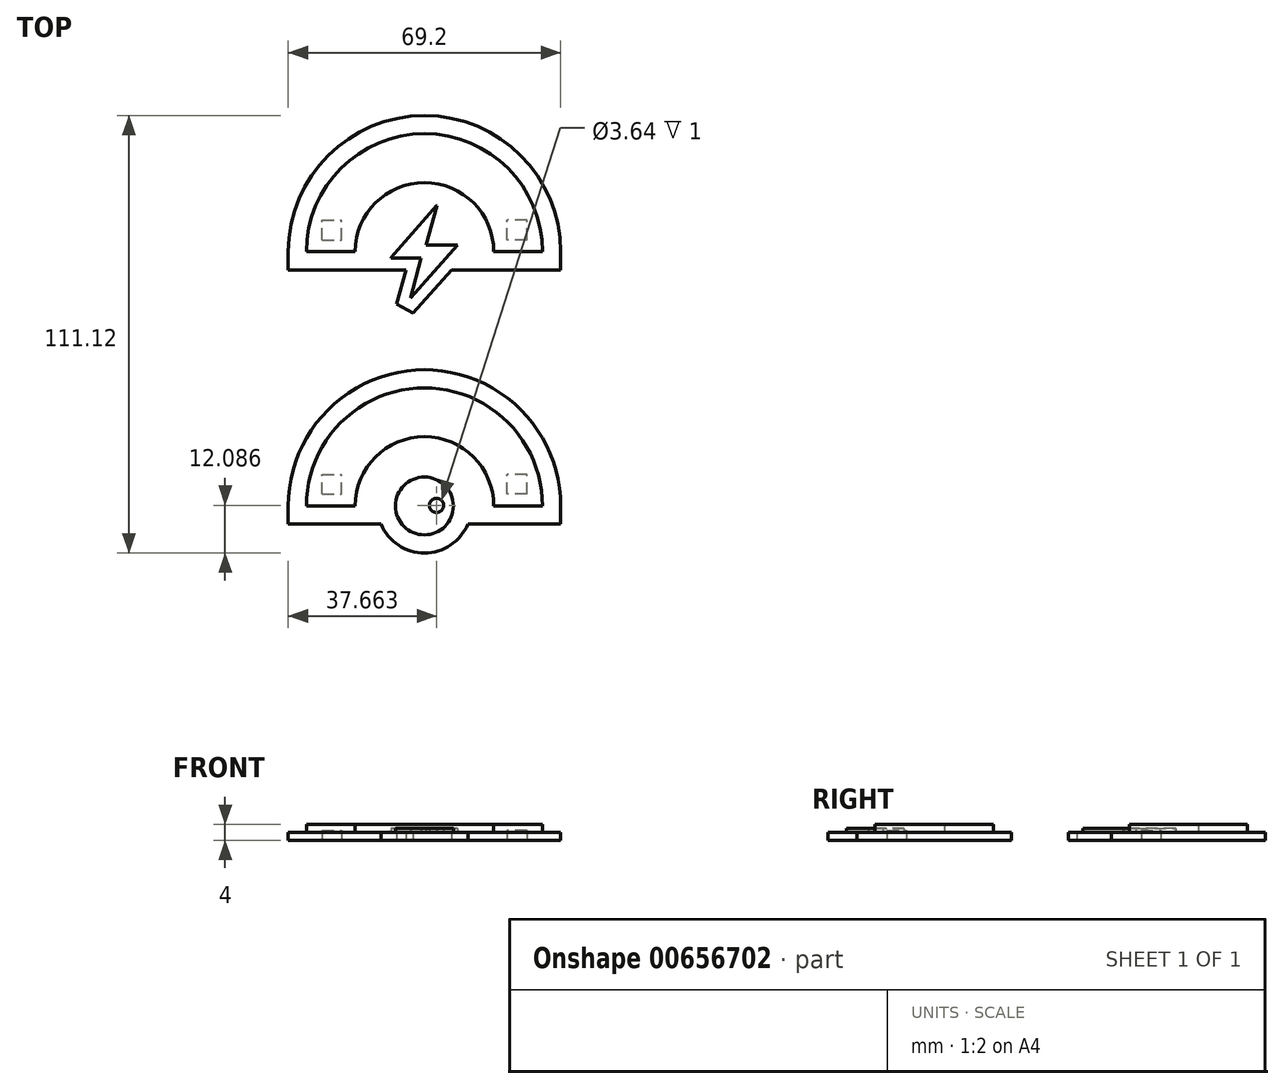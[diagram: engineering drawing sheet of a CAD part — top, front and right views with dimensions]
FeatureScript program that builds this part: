
annotation { "Feature Type Name" : "Feature", "Feature Type Description" : "" }
export const myFeature = defineFeature(function(context is Context, id is Id, definition is map)
    precondition{}
    {
        {
            var Q0;
            Q0=qCreatedBy(makeId("Top.planeOp"),FACE);
            var sketch = newSketch(context, id + "F0", { "sketchPlane" : qUnion([Q0])});
            skLineSegment(sketch, "E0", {"start": v(11.03, -48.21) * mm, "end": v(10.7, -49.01) * mm});
            skLineSegment(sketch, "E1", {"start": v(10.7, -49.01) * mm, "end": v(9.21, -51.22) * mm});
            skLineSegment(sketch, "E2", {"start": v(9.21, -51.22) * mm, "end": v(6.64, -53.54) * mm});
            skLineSegment(sketch, "E3", {"start": v(6.64, -53.54) * mm, "end": v(3.51, -55.03) * mm});
            skLineSegment(sketch, "E4", {"start": v(3.51, -55.03) * mm, "end": v(0.88, -55.56) * mm});
            skLineSegment(sketch, "E5", {"start": v(0.88, -55.56) * mm, "end": v(0, -55.56) * mm});
            skLineSegment(sketch, "E6", {"start": v(0, -55.56) * mm, "end": v(-0.88, -55.56) * mm});
            skLineSegment(sketch, "E7", {"start": v(-0.88, -55.56) * mm, "end": v(-3.52, -55.03) * mm});
            skLineSegment(sketch, "E8", {"start": v(-3.52, -55.03) * mm, "end": v(-6.65, -53.54) * mm});
            skLineSegment(sketch, "E9", {"start": v(-6.65, -53.54) * mm, "end": v(-9.22, -51.22) * mm});
            skLineSegment(sketch, "E10", {"start": v(-9.22, -51.22) * mm, "end": v(-10.7, -49.01) * mm});
            skLineSegment(sketch, "E11", {"start": v(-10.7, -49.01) * mm, "end": v(-11.03, -48.21) * mm});
            skLineSegment(sketch, "E12", {"start": v(-11.03, -48.21) * mm, "end": v(-34.6, -48.21) * mm});
            skLineSegment(sketch, "E13", {"start": v(-34.6, -48.21) * mm, "end": v(-34.6, -43.61) * mm});
            skLineSegment(sketch, "E14", {"start": v(-34.6, -43.61) * mm, "end": v(-34.6, -42.73) * mm});
            skLineSegment(sketch, "E15", {"start": v(-34.6, -42.73) * mm, "end": v(-34.42, -40.07) * mm});
            skLineSegment(sketch, "E16", {"start": v(-34.42, -40.07) * mm, "end": v(-33.9, -36.64) * mm});
            skLineSegment(sketch, "E17", {"start": v(-33.9, -36.64) * mm, "end": v(-33.05, -33.32) * mm});
            skLineSegment(sketch, "E18", {"start": v(-33.05, -33.32) * mm, "end": v(-31.88, -30.14) * mm});
            skLineSegment(sketch, "E19", {"start": v(-31.88, -30.14) * mm, "end": v(-30.43, -27.12) * mm});
            skLineSegment(sketch, "E20", {"start": v(-30.43, -27.12) * mm, "end": v(-28.7, -24.27) * mm});
            skLineSegment(sketch, "E21", {"start": v(-28.7, -24.27) * mm, "end": v(-26.7, -21.6) * mm});
            skLineSegment(sketch, "E22", {"start": v(-26.7, -21.6) * mm, "end": v(-24.47, -19.14) * mm});
            skLineSegment(sketch, "E23", {"start": v(-24.47, -19.14) * mm, "end": v(-22.01, -16.91) * mm});
            skLineSegment(sketch, "E24", {"start": v(-22.01, -16.91) * mm, "end": v(-19.35, -14.92) * mm});
            skLineSegment(sketch, "E25", {"start": v(-19.35, -14.92) * mm, "end": v(-16.5, -13.19) * mm});
            skLineSegment(sketch, "E26", {"start": v(-16.5, -13.19) * mm, "end": v(-13.47, -11.73) * mm});
            skLineSegment(sketch, "E27", {"start": v(-13.47, -11.73) * mm, "end": v(-10.29, -10.57) * mm});
            skLineSegment(sketch, "E28", {"start": v(-10.29, -10.57) * mm, "end": v(-6.97, -9.71) * mm});
            skLineSegment(sketch, "E29", {"start": v(-6.97, -9.71) * mm, "end": v(-3.54, -9.19) * mm});
            skLineSegment(sketch, "E30", {"start": v(-3.54, -9.19) * mm, "end": v(-0.88, -9.01) * mm});
            skLineSegment(sketch, "E31", {"start": v(-0.88, -9.01) * mm, "end": v(0, -9.01) * mm});
            skLineSegment(sketch, "E32", {"start": v(0, -9.01) * mm, "end": v(0.88, -9.01) * mm});
            skLineSegment(sketch, "E33", {"start": v(0.88, -9.01) * mm, "end": v(3.54, -9.19) * mm});
            skLineSegment(sketch, "E34", {"start": v(3.54, -9.19) * mm, "end": v(6.97, -9.71) * mm});
            skLineSegment(sketch, "E35", {"start": v(6.97, -9.71) * mm, "end": v(10.29, -10.57) * mm});
            skLineSegment(sketch, "E36", {"start": v(10.29, -10.57) * mm, "end": v(13.47, -11.73) * mm});
            skLineSegment(sketch, "E37", {"start": v(13.47, -11.73) * mm, "end": v(16.5, -13.19) * mm});
            skLineSegment(sketch, "E38", {"start": v(16.5, -13.19) * mm, "end": v(19.34, -14.92) * mm});
            skLineSegment(sketch, "E39", {"start": v(19.34, -14.92) * mm, "end": v(22, -16.91) * mm});
            skLineSegment(sketch, "E40", {"start": v(22, -16.91) * mm, "end": v(24.46, -19.14) * mm});
            skLineSegment(sketch, "E41", {"start": v(24.46, -19.14) * mm, "end": v(26.7, -21.6) * mm});
            skLineSegment(sketch, "E42", {"start": v(26.7, -21.6) * mm, "end": v(28.69, -24.27) * mm});
            skLineSegment(sketch, "E43", {"start": v(28.69, -24.27) * mm, "end": v(30.42, -27.12) * mm});
            skLineSegment(sketch, "E44", {"start": v(30.42, -27.12) * mm, "end": v(31.88, -30.14) * mm});
            skLineSegment(sketch, "E45", {"start": v(31.88, -30.14) * mm, "end": v(33.04, -33.32) * mm});
            skLineSegment(sketch, "E46", {"start": v(33.04, -33.32) * mm, "end": v(33.9, -36.64) * mm});
            skLineSegment(sketch, "E47", {"start": v(33.9, -36.64) * mm, "end": v(34.42, -40.07) * mm});
            skLineSegment(sketch, "E48", {"start": v(34.42, -40.07) * mm, "end": v(34.6, -42.73) * mm});
            skLineSegment(sketch, "E49", {"start": v(34.6, -42.73) * mm, "end": v(34.6, -43.61) * mm});
            skLineSegment(sketch, "E50", {"start": v(34.6, -43.61) * mm, "end": v(34.6, -48.21) * mm});
            skLineSegment(sketch, "E51", {"start": v(34.6, -48.21) * mm, "end": v(11.03, -48.21) * mm});
            skLineSegment(sketch, "E52", {"start": v(34.6, 20.97) * mm, "end": v(34.6, 21.86) * mm});
            skLineSegment(sketch, "E53", {"start": v(34.6, 21.86) * mm, "end": v(34.42, 24.5) * mm});
            skLineSegment(sketch, "E54", {"start": v(34.42, 24.5) * mm, "end": v(33.9, 27.94) * mm});
            skLineSegment(sketch, "E55", {"start": v(33.9, 27.94) * mm, "end": v(33.04, 31.26) * mm});
            skLineSegment(sketch, "E56", {"start": v(33.04, 31.26) * mm, "end": v(31.88, 34.44) * mm});
            skLineSegment(sketch, "E57", {"start": v(31.88, 34.44) * mm, "end": v(30.42, 37.46) * mm});
            skLineSegment(sketch, "E58", {"start": v(30.42, 37.46) * mm, "end": v(28.69, 40.31) * mm});
            skLineSegment(sketch, "E59", {"start": v(28.69, 40.31) * mm, "end": v(26.7, 42.97) * mm});
            skLineSegment(sketch, "E60", {"start": v(26.7, 42.97) * mm, "end": v(24.46, 45.43) * mm});
            skLineSegment(sketch, "E61", {"start": v(24.46, 45.43) * mm, "end": v(22, 47.66) * mm});
            skLineSegment(sketch, "E62", {"start": v(22, 47.66) * mm, "end": v(19.34, 49.65) * mm});
            skLineSegment(sketch, "E63", {"start": v(19.34, 49.65) * mm, "end": v(16.49, 51.39) * mm});
            skLineSegment(sketch, "E64", {"start": v(16.49, 51.39) * mm, "end": v(13.46, 52.84) * mm});
            skLineSegment(sketch, "E65", {"start": v(13.46, 52.84) * mm, "end": v(10.29, 54) * mm});
            skLineSegment(sketch, "E66", {"start": v(10.29, 54) * mm, "end": v(6.97, 54.86) * mm});
            skLineSegment(sketch, "E67", {"start": v(6.97, 54.86) * mm, "end": v(3.54, 55.38) * mm});
            skLineSegment(sketch, "E68", {"start": v(3.54, 55.38) * mm, "end": v(0.88, 55.56) * mm});
            skLineSegment(sketch, "E69", {"start": v(0.88, 55.56) * mm, "end": v(0, 55.56) * mm});
            skLineSegment(sketch, "E70", {"start": v(0, 55.56) * mm, "end": v(-0.88, 55.56) * mm});
            skLineSegment(sketch, "E71", {"start": v(-0.88, 55.56) * mm, "end": v(-3.54, 55.38) * mm});
            skLineSegment(sketch, "E72", {"start": v(-3.54, 55.38) * mm, "end": v(-6.97, 54.86) * mm});
            skLineSegment(sketch, "E73", {"start": v(-6.97, 54.86) * mm, "end": v(-10.29, 54) * mm});
            skLineSegment(sketch, "E74", {"start": v(-10.29, 54) * mm, "end": v(-13.46, 52.84) * mm});
            skLineSegment(sketch, "E75", {"start": v(-13.46, 52.84) * mm, "end": v(-16.49, 51.39) * mm});
            skLineSegment(sketch, "E76", {"start": v(-16.49, 51.39) * mm, "end": v(-19.34, 49.65) * mm});
            skLineSegment(sketch, "E77", {"start": v(-19.34, 49.65) * mm, "end": v(-22, 47.66) * mm});
            skLineSegment(sketch, "E78", {"start": v(-22, 47.66) * mm, "end": v(-24.46, 45.43) * mm});
            skLineSegment(sketch, "E79", {"start": v(-24.46, 45.43) * mm, "end": v(-26.7, 42.97) * mm});
            skLineSegment(sketch, "E80", {"start": v(-26.7, 42.97) * mm, "end": v(-28.69, 40.31) * mm});
            skLineSegment(sketch, "E81", {"start": v(-28.69, 40.31) * mm, "end": v(-30.42, 37.46) * mm});
            skLineSegment(sketch, "E82", {"start": v(-30.42, 37.46) * mm, "end": v(-31.88, 34.44) * mm});
            skLineSegment(sketch, "E83", {"start": v(-31.88, 34.44) * mm, "end": v(-33.04, 31.26) * mm});
            skLineSegment(sketch, "E84", {"start": v(-33.04, 31.26) * mm, "end": v(-33.9, 27.94) * mm});
            skLineSegment(sketch, "E85", {"start": v(-33.9, 27.94) * mm, "end": v(-34.42, 24.5) * mm});
            skLineSegment(sketch, "E86", {"start": v(-34.42, 24.5) * mm, "end": v(-34.6, 21.85) * mm});
            skLineSegment(sketch, "E87", {"start": v(-34.6, 21.85) * mm, "end": v(-34.6, 20.97) * mm});
            skLineSegment(sketch, "E88", {"start": v(-34.6, 20.97) * mm, "end": v(-34.6, 16.38) * mm});
            skLineSegment(sketch, "E89", {"start": v(-34.6, 16.38) * mm, "end": v(-4.72, 16.38) * mm});
            skLineSegment(sketch, "E90", {"start": v(-4.72, 16.38) * mm, "end": v(-7.03, 7.7) * mm});
            skLineSegment(sketch, "E91", {"start": v(-7.03, 7.7) * mm, "end": v(-2.86, 5.45) * mm});
            skLineSegment(sketch, "E92", {"start": v(-2.86, 5.45) * mm, "end": v(6.87, 16.38) * mm});
            skLineSegment(sketch, "E93", {"start": v(6.87, 16.38) * mm, "end": v(34.6, 16.38) * mm});
            skLineSegment(sketch, "E94", {"start": v(34.6, 16.38) * mm, "end": v(34.6, 20.97) * mm});
            skLineSegment(sketch, "E95", {"start": v(-0.82, 19.38) * mm, "end": v(-3.52, 9.21) * mm});
            skLineSegment(sketch, "E96", {"start": v(-3.52, 9.21) * mm, "end": v(-3.48, 9.19) * mm});
            skLineSegment(sketch, "E97", {"start": v(-3.48, 9.19) * mm, "end": v(8.47, 22.68) * mm});
            skLineSegment(sketch, "E98", {"start": v(8.47, 22.68) * mm, "end": v(0.43, 22.68) * mm});
            skLineSegment(sketch, "E99", {"start": v(0.43, 22.68) * mm, "end": v(3.15, 32.7) * mm});
            skLineSegment(sketch, "E100", {"start": v(3.15, 32.7) * mm, "end": v(3.08, 32.73) * mm});
            skLineSegment(sketch, "E101", {"start": v(3.08, 32.73) * mm, "end": v(-8.47, 19.51) * mm});
            skLineSegment(sketch, "E102", {"start": v(-8.47, 19.51) * mm, "end": v(-8.42, 19.38) * mm});
            skLineSegment(sketch, "E103", {"start": v(-8.42, 19.38) * mm, "end": v(-0.82, 19.38) * mm});
            skLineSegment(sketch, "E104", {"start": v(-0.01, 50.96) * mm, "end": v(-1.52, 50.96) * mm});
            skLineSegment(sketch, "E105", {"start": v(-1.52, 50.96) * mm, "end": v(-6.06, 50.35) * mm});
            skLineSegment(sketch, "E106", {"start": v(-6.06, 50.35) * mm, "end": v(-11.69, 48.6) * mm});
            skLineSegment(sketch, "E107", {"start": v(-11.69, 48.6) * mm, "end": v(-16.78, 45.84) * mm});
            skLineSegment(sketch, "E108", {"start": v(-16.78, 45.84) * mm, "end": v(-21.22, 42.18) * mm});
            skLineSegment(sketch, "E109", {"start": v(-21.22, 42.18) * mm, "end": v(-24.88, 37.74) * mm});
            skLineSegment(sketch, "E110", {"start": v(-24.88, 37.74) * mm, "end": v(-27.64, 32.65) * mm});
            skLineSegment(sketch, "E111", {"start": v(-27.64, 32.65) * mm, "end": v(-29.4, 27.02) * mm});
            skLineSegment(sketch, "E112", {"start": v(-29.4, 27.02) * mm, "end": v(-30, 22.48) * mm});
            skLineSegment(sketch, "E113", {"start": v(-30, 22.48) * mm, "end": v(-30, 20.97) * mm});
            skLineSegment(sketch, "E114", {"start": v(-30, 20.97) * mm, "end": v(-17.62, 20.97) * mm});
            skLineSegment(sketch, "E115", {"start": v(-17.62, 20.97) * mm, "end": v(-17.62, 21.86) * mm});
            skLineSegment(sketch, "E116", {"start": v(-17.62, 21.86) * mm, "end": v(-17.26, 24.51) * mm});
            skLineSegment(sketch, "E117", {"start": v(-17.26, 24.51) * mm, "end": v(-16.23, 27.81) * mm});
            skLineSegment(sketch, "E118", {"start": v(-16.23, 27.81) * mm, "end": v(-14.6, 30.8) * mm});
            skLineSegment(sketch, "E119", {"start": v(-14.6, 30.8) * mm, "end": v(-12.45, 33.4) * mm});
            skLineSegment(sketch, "E120", {"start": v(-12.45, 33.4) * mm, "end": v(-9.85, 35.55) * mm});
            skLineSegment(sketch, "E121", {"start": v(-9.85, 35.55) * mm, "end": v(-6.86, 37.17) * mm});
            skLineSegment(sketch, "E122", {"start": v(-6.86, 37.17) * mm, "end": v(-3.55, 38.2) * mm});
            skLineSegment(sketch, "E123", {"start": v(-3.55, 38.2) * mm, "end": v(-0.9, 38.55) * mm});
            skLineSegment(sketch, "E124", {"start": v(-0.9, 38.55) * mm, "end": v(-0.01, 38.55) * mm});
            skLineSegment(sketch, "E125", {"start": v(-0.01, 38.55) * mm, "end": v(0.88, 38.55) * mm});
            skLineSegment(sketch, "E126", {"start": v(0.88, 38.55) * mm, "end": v(3.54, 38.2) * mm});
            skLineSegment(sketch, "E127", {"start": v(3.54, 38.2) * mm, "end": v(6.84, 37.17) * mm});
            skLineSegment(sketch, "E128", {"start": v(6.84, 37.17) * mm, "end": v(9.83, 35.55) * mm});
            skLineSegment(sketch, "E129", {"start": v(9.83, 35.55) * mm, "end": v(12.44, 33.4) * mm});
            skLineSegment(sketch, "E130", {"start": v(12.44, 33.4) * mm, "end": v(14.59, 30.8) * mm});
            skLineSegment(sketch, "E131", {"start": v(14.59, 30.8) * mm, "end": v(16.21, 27.81) * mm});
            skLineSegment(sketch, "E132", {"start": v(16.21, 27.81) * mm, "end": v(17.24, 24.51) * mm});
            skLineSegment(sketch, "E133", {"start": v(17.24, 24.51) * mm, "end": v(17.6, 21.86) * mm});
            skLineSegment(sketch, "E134", {"start": v(17.6, 21.86) * mm, "end": v(17.6, 20.97) * mm});
            skLineSegment(sketch, "E135", {"start": v(17.6, 20.97) * mm, "end": v(30, 20.97) * mm});
            skLineSegment(sketch, "E136", {"start": v(30, 20.97) * mm, "end": v(30, 22.48) * mm});
            skLineSegment(sketch, "E137", {"start": v(30, 22.48) * mm, "end": v(29.39, 27.02) * mm});
            skLineSegment(sketch, "E138", {"start": v(29.39, 27.02) * mm, "end": v(27.64, 32.65) * mm});
            skLineSegment(sketch, "E139", {"start": v(27.64, 32.65) * mm, "end": v(24.87, 37.74) * mm});
            skLineSegment(sketch, "E140", {"start": v(24.87, 37.74) * mm, "end": v(21.2, 42.18) * mm});
            skLineSegment(sketch, "E141", {"start": v(21.2, 42.18) * mm, "end": v(16.76, 45.84) * mm});
            skLineSegment(sketch, "E142", {"start": v(16.76, 45.84) * mm, "end": v(11.67, 48.6) * mm});
            skLineSegment(sketch, "E143", {"start": v(11.67, 48.6) * mm, "end": v(6.03, 50.35) * mm});
            skLineSegment(sketch, "E144", {"start": v(6.03, 50.35) * mm, "end": v(1.5, 50.96) * mm});
            skLineSegment(sketch, "E145", {"start": v(1.5, 50.96) * mm, "end": v(-0.01, 50.96) * mm});
            skLineSegment(sketch, "E146", {"start": v(0, -13.6) * mm, "end": v(-1.51, -13.6) * mm});
            skLineSegment(sketch, "E147", {"start": v(-1.51, -13.6) * mm, "end": v(-6.05, -14.22) * mm});
            skLineSegment(sketch, "E148", {"start": v(-6.05, -14.22) * mm, "end": v(-11.68, -15.97) * mm});
            skLineSegment(sketch, "E149", {"start": v(-11.68, -15.97) * mm, "end": v(-16.77, -18.73) * mm});
            skLineSegment(sketch, "E150", {"start": v(-16.77, -18.73) * mm, "end": v(-21.21, -22.4) * mm});
            skLineSegment(sketch, "E151", {"start": v(-21.21, -22.4) * mm, "end": v(-24.88, -26.83) * mm});
            skLineSegment(sketch, "E152", {"start": v(-24.88, -26.83) * mm, "end": v(-27.64, -31.93) * mm});
            skLineSegment(sketch, "E153", {"start": v(-27.64, -31.93) * mm, "end": v(-29.4, -37.56) * mm});
            skLineSegment(sketch, "E154", {"start": v(-29.4, -37.56) * mm, "end": v(-30, -42.1) * mm});
            skLineSegment(sketch, "E155", {"start": v(-30, -42.1) * mm, "end": v(-30, -43.61) * mm});
            skLineSegment(sketch, "E156", {"start": v(-30, -43.61) * mm, "end": v(-17.6, -43.61) * mm});
            skLineSegment(sketch, "E157", {"start": v(-17.6, -43.61) * mm, "end": v(-17.6, -42.72) * mm});
            skLineSegment(sketch, "E158", {"start": v(-17.6, -42.72) * mm, "end": v(-17.25, -40.06) * mm});
            skLineSegment(sketch, "E159", {"start": v(-17.25, -40.06) * mm, "end": v(-16.22, -36.76) * mm});
            skLineSegment(sketch, "E160", {"start": v(-16.22, -36.76) * mm, "end": v(-14.6, -33.77) * mm});
            skLineSegment(sketch, "E161", {"start": v(-14.6, -33.77) * mm, "end": v(-12.45, -31.16) * mm});
            skLineSegment(sketch, "E162", {"start": v(-12.45, -31.16) * mm, "end": v(-9.84, -29.01) * mm});
            skLineSegment(sketch, "E163", {"start": v(-9.84, -29.01) * mm, "end": v(-6.85, -27.4) * mm});
            skLineSegment(sketch, "E164", {"start": v(-6.85, -27.4) * mm, "end": v(-3.55, -26.37) * mm});
            skLineSegment(sketch, "E165", {"start": v(-3.55, -26.37) * mm, "end": v(-0.9, -26) * mm});
            skLineSegment(sketch, "E166", {"start": v(-0.9, -26) * mm, "end": v(0, -26) * mm});
            skLineSegment(sketch, "E167", {"start": v(0, -26) * mm, "end": v(0.88, -26) * mm});
            skLineSegment(sketch, "E168", {"start": v(0.88, -26) * mm, "end": v(3.54, -26.37) * mm});
            skLineSegment(sketch, "E169", {"start": v(3.54, -26.37) * mm, "end": v(6.85, -27.4) * mm});
            skLineSegment(sketch, "E170", {"start": v(6.85, -27.4) * mm, "end": v(9.84, -29.01) * mm});
            skLineSegment(sketch, "E171", {"start": v(9.84, -29.01) * mm, "end": v(12.45, -31.16) * mm});
            skLineSegment(sketch, "E172", {"start": v(12.45, -31.16) * mm, "end": v(14.6, -33.77) * mm});
            skLineSegment(sketch, "E173", {"start": v(14.6, -33.77) * mm, "end": v(16.22, -36.76) * mm});
            skLineSegment(sketch, "E174", {"start": v(16.22, -36.76) * mm, "end": v(17.25, -40.06) * mm});
            skLineSegment(sketch, "E175", {"start": v(17.25, -40.06) * mm, "end": v(17.6, -42.72) * mm});
            skLineSegment(sketch, "E176", {"start": v(17.6, -42.72) * mm, "end": v(17.6, -43.61) * mm});
            skLineSegment(sketch, "E177", {"start": v(17.6, -43.61) * mm, "end": v(30, -43.61) * mm});
            skLineSegment(sketch, "E178", {"start": v(30, -43.61) * mm, "end": v(30, -42.1) * mm});
            skLineSegment(sketch, "E179", {"start": v(30, -42.1) * mm, "end": v(29.39, -37.56) * mm});
            skLineSegment(sketch, "E180", {"start": v(29.39, -37.56) * mm, "end": v(27.64, -31.93) * mm});
            skLineSegment(sketch, "E181", {"start": v(27.64, -31.93) * mm, "end": v(24.88, -26.83) * mm});
            skLineSegment(sketch, "E182", {"start": v(24.88, -26.83) * mm, "end": v(21.21, -22.4) * mm});
            skLineSegment(sketch, "E183", {"start": v(21.21, -22.4) * mm, "end": v(16.77, -18.73) * mm});
            skLineSegment(sketch, "E184", {"start": v(16.77, -18.73) * mm, "end": v(11.68, -15.97) * mm});
            skLineSegment(sketch, "E185", {"start": v(11.68, -15.97) * mm, "end": v(6.05, -14.22) * mm});
            skLineSegment(sketch, "E186", {"start": v(6.05, -14.22) * mm, "end": v(1.51, -13.6) * mm});
            skLineSegment(sketch, "E187", {"start": v(1.51, -13.6) * mm, "end": v(0, -13.6) * mm});
            skLineSegment(sketch, "E188", {"start": v(7.35, -43.61) * mm, "end": v(7.35, -44.33) * mm});
            skLineSegment(sketch, "E189", {"start": v(7.35, -44.33) * mm, "end": v(6.77, -46.47) * mm});
            skLineSegment(sketch, "E190", {"start": v(6.77, -46.47) * mm, "end": v(5.2, -48.8) * mm});
            skLineSegment(sketch, "E191", {"start": v(5.2, -48.8) * mm, "end": v(2.86, -50.38) * mm});
            skLineSegment(sketch, "E192", {"start": v(2.86, -50.38) * mm, "end": v(0.71, -50.96) * mm});
            skLineSegment(sketch, "E193", {"start": v(0.71, -50.96) * mm, "end": v(0, -50.96) * mm});
            skLineSegment(sketch, "E194", {"start": v(0, -50.96) * mm, "end": v(-0.72, -50.96) * mm});
            skLineSegment(sketch, "E195", {"start": v(-0.72, -50.96) * mm, "end": v(-2.86, -50.38) * mm});
            skLineSegment(sketch, "E196", {"start": v(-2.86, -50.38) * mm, "end": v(-5.2, -48.8) * mm});
            skLineSegment(sketch, "E197", {"start": v(-5.2, -48.8) * mm, "end": v(-6.77, -46.47) * mm});
            skLineSegment(sketch, "E198", {"start": v(-6.77, -46.47) * mm, "end": v(-7.35, -44.33) * mm});
            skLineSegment(sketch, "E199", {"start": v(-7.35, -44.33) * mm, "end": v(-7.35, -43.61) * mm});
            skLineSegment(sketch, "E200", {"start": v(-7.35, -43.61) * mm, "end": v(-7.35, -42.9) * mm});
            skLineSegment(sketch, "E201", {"start": v(-7.35, -42.9) * mm, "end": v(-6.77, -40.75) * mm});
            skLineSegment(sketch, "E202", {"start": v(-6.77, -40.75) * mm, "end": v(-5.2, -38.41) * mm});
            skLineSegment(sketch, "E203", {"start": v(-5.2, -38.41) * mm, "end": v(-2.86, -36.84) * mm});
            skLineSegment(sketch, "E204", {"start": v(-2.86, -36.84) * mm, "end": v(-0.72, -36.26) * mm});
            skLineSegment(sketch, "E205", {"start": v(-0.72, -36.26) * mm, "end": v(0, -36.26) * mm});
            skLineSegment(sketch, "E206", {"start": v(0, -36.26) * mm, "end": v(0.71, -36.26) * mm});
            skLineSegment(sketch, "E207", {"start": v(0.71, -36.26) * mm, "end": v(2.86, -36.84) * mm});
            skLineSegment(sketch, "E208", {"start": v(2.86, -36.84) * mm, "end": v(5.2, -38.41) * mm});
            skLineSegment(sketch, "E209", {"start": v(5.2, -38.41) * mm, "end": v(6.77, -40.75) * mm});
            skLineSegment(sketch, "E210", {"start": v(6.77, -40.75) * mm, "end": v(7.35, -42.9) * mm});
            skLineSegment(sketch, "E211", {"start": v(7.35, -42.9) * mm, "end": v(7.35, -43.61) * mm});
            skLineSegment(sketch, "E212", {"start": v(1.24, -43.47) * mm, "end": v(1.24, -43.3) * mm});
            skLineSegment(sketch, "E213", {"start": v(1.24, -43.3) * mm, "end": v(1.39, -42.77) * mm});
            skLineSegment(sketch, "E214", {"start": v(1.39, -42.77) * mm, "end": v(1.78, -42.19) * mm});
            skLineSegment(sketch, "E215", {"start": v(1.78, -42.19) * mm, "end": v(2.36, -41.8) * mm});
            skLineSegment(sketch, "E216", {"start": v(2.36, -41.8) * mm, "end": v(2.89, -41.65) * mm});
            skLineSegment(sketch, "E217", {"start": v(2.89, -41.65) * mm, "end": v(3.07, -41.65) * mm});
            skLineSegment(sketch, "E218", {"start": v(3.07, -41.65) * mm, "end": v(3.24, -41.65) * mm});
            skLineSegment(sketch, "E219", {"start": v(3.24, -41.65) * mm, "end": v(3.77, -41.8) * mm});
            skLineSegment(sketch, "E220", {"start": v(3.77, -41.8) * mm, "end": v(4.35, -42.19) * mm});
            skLineSegment(sketch, "E221", {"start": v(4.35, -42.19) * mm, "end": v(4.74, -42.77) * mm});
            skLineSegment(sketch, "E222", {"start": v(4.74, -42.77) * mm, "end": v(4.88, -43.3) * mm});
            skLineSegment(sketch, "E223", {"start": v(4.88, -43.3) * mm, "end": v(4.88, -43.47) * mm});
            skLineSegment(sketch, "E224", {"start": v(4.88, -43.47) * mm, "end": v(4.88, -43.65) * mm});
            skLineSegment(sketch, "E225", {"start": v(4.88, -43.65) * mm, "end": v(4.74, -44.18) * mm});
            skLineSegment(sketch, "E226", {"start": v(4.74, -44.18) * mm, "end": v(4.35, -44.76) * mm});
            skLineSegment(sketch, "E227", {"start": v(4.35, -44.76) * mm, "end": v(3.77, -45.15) * mm});
            skLineSegment(sketch, "E228", {"start": v(3.77, -45.15) * mm, "end": v(3.24, -45.3) * mm});
            skLineSegment(sketch, "E229", {"start": v(3.24, -45.3) * mm, "end": v(3.07, -45.3) * mm});
            skLineSegment(sketch, "E230", {"start": v(3.07, -45.3) * mm, "end": v(2.89, -45.3) * mm});
            skLineSegment(sketch, "E231", {"start": v(2.89, -45.3) * mm, "end": v(2.36, -45.15) * mm});
            skLineSegment(sketch, "E232", {"start": v(2.36, -45.15) * mm, "end": v(1.78, -44.76) * mm});
            skLineSegment(sketch, "E233", {"start": v(1.78, -44.76) * mm, "end": v(1.39, -44.18) * mm});
            skLineSegment(sketch, "E234", {"start": v(1.39, -44.18) * mm, "end": v(1.24, -43.65) * mm});
            skLineSegment(sketch, "E235", {"start": v(1.24, -43.65) * mm, "end": v(1.24, -43.47) * mm});
            skSolve(sketch);
        }
        {
            var Q0;
            Q0=qCreatedBy(makeId("Top.planeOp"),FACE);
            var sketch = newSketch(context, id + "F1", { "sketchPlane" : qUnion([Q0])});
            skPoint(sketch, "E236.0", {"position": v(-34.6, 20.97) * mm});
            skPoint(sketch, "E237.0", {"position": v(-34.6, 16.38) * mm});
            skPoint(sketch, "E238.0", {"position": v(-4.72, 16.38) * mm});
            skPoint(sketch, "E239.0", {"position": v(-7.03, 7.7) * mm});
            skPoint(sketch, "E240.0", {"position": v(-2.86, 5.45) * mm});
            skPoint(sketch, "E241.0", {"position": v(6.87, 16.38) * mm});
            skPoint(sketch, "E242.0", {"position": v(34.6, 16.38) * mm});
            skPoint(sketch, "E243.0", {"position": v(34.6, 20.97) * mm});
            skPoint(sketch, "E244.0", {"position": v(0, 55.56) * mm});
            skPoint(sketch, "E245.0", {"position": v(-0.01, 50.96) * mm});
            skPoint(sketch, "E246.0", {"position": v(-30, 20.97) * mm});
            skPoint(sketch, "E247.0", {"position": v(-17.62, 20.97) * mm});
            skPoint(sketch, "E248.0", {"position": v(-0.01, 38.55) * mm});
            skPoint(sketch, "E249.0", {"position": v(17.6, 20.97) * mm});
            skPoint(sketch, "E250.0", {"position": v(30, 20.97) * mm});
            skPoint(sketch, "E251.0", {"position": v(3.08, 32.73) * mm});
            skPoint(sketch, "E252.0", {"position": v(3.15, 32.7) * mm});
            skPoint(sketch, "E253.0", {"position": v(0.43, 22.68) * mm});
            skPoint(sketch, "E254.0", {"position": v(8.47, 22.68) * mm});
            skPoint(sketch, "E255.0", {"position": v(-3.48, 9.19) * mm});
            skPoint(sketch, "E256.0", {"position": v(-3.52, 9.21) * mm});
            skPoint(sketch, "E257.0", {"position": v(-0.82, 19.38) * mm});
            skPoint(sketch, "E258.0", {"position": v(-8.42, 19.38) * mm});
            skPoint(sketch, "E259.0", {"position": v(-8.47, 19.51) * mm});
            skLineSegment(sketch, "E260.0", {"start": v(-8.47, 19.51) * mm, "end": v(-8.42, 19.38) * mm});
            skLineSegment(sketch, "E261.0", {"start": v(-8.42, 19.38) * mm, "end": v(-0.82, 19.38) * mm});
            skLineSegment(sketch, "E262.0", {"start": v(3.08, 32.73) * mm, "end": v(-8.47, 19.51) * mm});
            skLineSegment(sketch, "E263.0", {"start": v(3.15, 32.7) * mm, "end": v(3.08, 32.73) * mm});
            skLineSegment(sketch, "E264.0", {"start": v(0.43, 22.68) * mm, "end": v(3.15, 32.7) * mm});
            skLineSegment(sketch, "E265.0", {"start": v(8.47, 22.68) * mm, "end": v(0.43, 22.68) * mm});
            skLineSegment(sketch, "E266.0", {"start": v(-3.48, 9.19) * mm, "end": v(8.47, 22.68) * mm});
            skLineSegment(sketch, "E267.0", {"start": v(-0.82, 19.38) * mm, "end": v(-3.52, 9.21) * mm});
            skLineSegment(sketch, "E268.0", {"start": v(-34.6, 16.38) * mm, "end": v(-4.72, 16.38) * mm});
            skLineSegment(sketch, "E269.0", {"start": v(6.87, 16.38) * mm, "end": v(34.6, 16.38) * mm});
            skLineSegment(sketch, "E270.0", {"start": v(-2.86, 5.45) * mm, "end": v(6.87, 16.38) * mm});
            skLineSegment(sketch, "E271.0", {"start": v(-7.03, 7.7) * mm, "end": v(-2.86, 5.45) * mm});
            skLineSegment(sketch, "E272.0", {"start": v(-4.72, 16.38) * mm, "end": v(-7.03, 7.7) * mm});
            skLineSegment(sketch, "E273.0", {"start": v(-34.6, 20.97) * mm, "end": v(-34.6, 16.38) * mm});
            skLineSegment(sketch, "E274.0", {"start": v(34.6, 16.38) * mm, "end": v(34.6, 20.97) * mm});
            skLineSegment(sketch, "E275.0", {"start": v(-30, 20.97) * mm, "end": v(-17.62, 20.97) * mm});
            skLineSegment(sketch, "E276.0", {"start": v(17.6, 20.97) * mm, "end": v(30, 20.97) * mm});
            skArc(sketch, "E277", {"start": v(34.6, 20.97) * mm, "mid": v(0, 55.56) * mm, "end": v(-34.6, 20.97) * mm});
            skArc(sketch, "E278", {"start": v(30, 20.97) * mm, "mid": v(0, 50.96) * mm, "end": v(-30, 20.97) * mm});
            skArc(sketch, "E279", {"start": v(17.6, 20.97) * mm, "mid": v(-0.01, 38.55) * mm, "end": v(-17.62, 20.97) * mm});
            skLineSegment(sketch, "E280", {"start": v(-3.52, 9.21) * mm, "end": v(-3.48, 9.19) * mm});
            skSolve(sketch);
        }
        {
            var Q0;
            Q0=qCreatedBy(makeId("Top.planeOp"),FACE);
            var sketch = newSketch(context, id + "F2", { "sketchPlane" : qUnion([Q0])});
            skPoint(sketch, "E281.0", {"position": v(-34.6, -48.21) * mm});
            skPoint(sketch, "E282.0", {"position": v(-11.03, -48.21) * mm});
            skPoint(sketch, "E283.0", {"position": v(11.03, -48.21) * mm});
            skPoint(sketch, "E284.0", {"position": v(34.6, -48.21) * mm});
            skPoint(sketch, "E285.0", {"position": v(0, -9.01) * mm});
            skPoint(sketch, "E286.0", {"position": v(0, -13.6) * mm});
            skPoint(sketch, "E287.0", {"position": v(0, -26) * mm});
            skPoint(sketch, "E288.0", {"position": v(0, -36.26) * mm});
            skPoint(sketch, "E289.0", {"position": v(0, -50.96) * mm});
            skPoint(sketch, "E290.0", {"position": v(0, -55.56) * mm});
            skPoint(sketch, "E291.0", {"position": v(-7.35, -43.61) * mm});
            skPoint(sketch, "E292.0", {"position": v(7.35, -43.61) * mm});
            skPoint(sketch, "E293.0", {"position": v(3.07, -41.65) * mm});
            skPoint(sketch, "E294.0", {"position": v(1.24, -43.47) * mm});
            skPoint(sketch, "E295.0", {"position": v(4.88, -43.47) * mm});
            skPoint(sketch, "E296.0", {"position": v(3.07, -45.3) * mm});
            skPoint(sketch, "E297.0", {"position": v(-17.6, -43.61) * mm});
            skPoint(sketch, "E298.0", {"position": v(-30, -43.61) * mm});
            skLineSegment(sketch, "E299.0", {"start": v(-30, -43.61) * mm, "end": v(-17.6, -43.61) * mm});
            skLineSegment(sketch, "E300.0", {"start": v(-11.03, -48.21) * mm, "end": v(-34.6, -48.21) * mm});
            skLineSegment(sketch, "E301.0", {"start": v(17.6, -43.61) * mm, "end": v(30, -43.61) * mm});
            skLineSegment(sketch, "E302.0", {"start": v(34.6, -48.21) * mm, "end": v(11.03, -48.21) * mm});
            skLineSegment(sketch, "E303.0", {"start": v(-34.6, -48.21) * mm, "end": v(-34.6, -43.61) * mm});
            skLineSegment(sketch, "E304.0", {"start": v(34.6, -43.61) * mm, "end": v(34.6, -48.21) * mm});
            skArc(sketch, "E305", {"start": v(34.6, -43.61) * mm, "mid": v(0, -9.01) * mm, "end": v(-34.6, -43.61) * mm});
            skArc(sketch, "E306", {"start": v(30, -43.61) * mm, "mid": v(0, -13.6) * mm, "end": v(-30, -43.61) * mm});
            skArc(sketch, "E307", {"start": v(17.6, -43.61) * mm, "mid": v(0, -26) * mm, "end": v(-17.6, -43.61) * mm});
            skArc(sketch, "E308", {"start": v(-11.03, -48.21) * mm, "mid": v(0, -55.56) * mm, "end": v(11.03, -48.21) * mm});
            skCircle(sketch, "E309", {"center": v(0, -43.61) * mm, "radius": 7.35 * mm});
            skCircle(sketch, "E310", {"center": v(3.06, -43.47) * mm, "radius": 1.82 * mm});
            skSolve(sketch);
        }
        {
            var Q0;
            Q0=makeQuery(id+"F1.imprint","IMPRINT",FACE,{"disambiguationData":[TD([[makeQuery(id+"F1.imprint","IMPRINT",EDGE,{"derivedFrom":sQuery(id+"F1.wireOp",EDGE,"E268.0")}),1.0]])]});
            var Q1;
            Q1=makeQuery(id+"F1.imprint","IMPRINT",FACE,{"disambiguationData":[TD([[makeQuery(id+"F1.imprint","IMPRINT",EDGE,{"derivedFrom":sQuery(id+"F1.wireOp",EDGE,"E275.0")}),1.0]])]});
            extrude(context, id + "F3", {"entities" : qUnion([Q0, Q1]), "depth" : 2 * mm, "offsetDistance" : 25 * mm});
        }
        {
            var Q0;
            Q0=makeQuery(id+"F1.imprint","IMPRINT",FACE,{"disambiguationData":[TD([[makeQuery(id+"F1.imprint","IMPRINT",EDGE,{"derivedFrom":sQuery(id+"F1.wireOp",EDGE,"E275.0")}),1.0]])]});
            extrude(context, id + "F4", {"entities" : qUnion([Q0]), "operationType" : NewBodyOperationType.ADD, "depth" : 4 * mm, "offsetDistance" : 25 * mm});
        }
        {
            var Q0;
            Q0=makeQuery(id+"F1.imprint","IMPRINT",FACE,{"disambiguationData":[TD([[makeQuery(id+"F1.imprint","IMPRINT",EDGE,{"derivedFrom":sQuery(id+"F1.wireOp",EDGE,"E260.0")}),1.0]])]});
            extrude(context, id + "F5", {"entities" : qUnion([Q0]), "operationType" : NewBodyOperationType.ADD, "depth" : 3 * mm, "offsetDistance" : 25 * mm});
        }
        {
            var Q0;
            Q0=makeQuery(id+"F2.imprint","IMPRINT",FACE,{"disambiguationData":[TD([[makeQuery(id+"F2.imprint","IMPRINT",EDGE,{"derivedFrom":sQuery(id+"F2.wireOp",EDGE,"E299.0")}),1.0]])]});
            var Q1;
            Q1=makeQuery(id+"F2.imprint","IMPRINT",FACE,{"disambiguationData":[TD([[makeQuery(id+"F2.imprint","IMPRINT",EDGE,{"derivedFrom":sQuery(id+"F2.wireOp",EDGE,"E299.0")}),-1.0]])]});
            var Q2;
            Q2=makeQuery(id+"F2.imprint","IMPRINT",FACE,{"disambiguationData":[TD([[makeQuery(id+"F2.imprint","IMPRINT",EDGE,{"derivedFrom":sQuery(id+"F2.wireOp",EDGE,"E309")}),1.0]])]});
            var Q3;
            Q3=makeQuery(id+"F2.imprint","IMPRINT",FACE,{"disambiguationData":[TD([[makeQuery(id+"F2.imprint","IMPRINT",EDGE,{"derivedFrom":sQuery(id+"F2.wireOp",EDGE,"E310")}),1.0]])]});
            extrude(context, id + "F6", {"entities" : qUnion([Q0, Q1, Q2, Q3]), "depth" : 2 * mm, "offsetDistance" : 25 * mm});
        }
        {
            var Q0;
            Q0=makeQuery(id+"F2.imprint","IMPRINT",FACE,{"disambiguationData":[TD([[makeQuery(id+"F2.imprint","IMPRINT",EDGE,{"derivedFrom":sQuery(id+"F2.wireOp",EDGE,"E299.0")}),1.0]])]});
            extrude(context, id + "F7", {"entities" : qUnion([Q0]), "operationType" : NewBodyOperationType.ADD, "depth" : 4 * mm, "offsetDistance" : 25 * mm});
        }
        {
            var Q0;
            Q0=makeQuery(id+"F2.imprint","IMPRINT",FACE,{"disambiguationData":[TD([[makeQuery(id+"F2.imprint","IMPRINT",EDGE,{"derivedFrom":sQuery(id+"F2.wireOp",EDGE,"E309")}),1.0]])]});
            extrude(context, id + "F8", {"entities" : qUnion([Q0]), "operationType" : NewBodyOperationType.ADD, "depth" : 3 * mm, "offsetDistance" : 25 * mm});
        }
        {
            var Q0;
            Q0=qCreatedBy(makeId("Top.planeOp"),FACE);
            var sketch = newSketch(context, id + "F9", { "sketchPlane" : qUnion([Q0])});
            skLineSegment(sketch, "E311.bottom", {"start": v(-26, -40.61) * mm, "end": v(-21, -40.61) * mm});
            skLineSegment(sketch, "E311.top", {"start": v(-26, -35.61) * mm, "end": v(-21, -35.61) * mm});
            skLineSegment(sketch, "E311.left", {"start": v(-26, -40.61) * mm, "end": v(-26, -35.61) * mm});
            skLineSegment(sketch, "E311.right", {"start": v(-21, -40.61) * mm, "end": v(-21, -35.61) * mm});
            skLineSegment(sketch, "E312.bottom", {"start": v(0, -22) * mm, "end": v(-2.5, -22) * mm});
            skLineSegment(sketch, "E312.top", {"start": v(0, -17) * mm, "end": v(-2.5, -17) * mm});
            skLineSegment(sketch, "E312.right", {"start": v(-2.5, -22) * mm, "end": v(-2.5, -17) * mm});
            skLineSegment(sketch, "E313.MirrorCS", {"start": v(0, -22) * mm, "end": v(2.5, -22) * mm});
            skLineSegment(sketch, "E314.MirrorCS", {"start": v(2.5, -22) * mm, "end": v(2.5, -17) * mm});
            skLineSegment(sketch, "E315.MirrorCS", {"start": v(0, -17) * mm, "end": v(2.5, -17) * mm});
            skLineSegment(sketch, "E316.MirrorCS", {"start": v(26, -35.61) * mm, "end": v(21, -35.61) * mm});
            skLineSegment(sketch, "E317.MirrorCS", {"start": v(26, -40.61) * mm, "end": v(26, -35.61) * mm});
            skLineSegment(sketch, "E318.MirrorCS", {"start": v(26, -40.61) * mm, "end": v(21, -40.61) * mm});
            skLineSegment(sketch, "E319.MirrorCS", {"start": v(21, -40.61) * mm, "end": v(21, -35.61) * mm});
            skPoint(sketch, "E320.0", {"position": v(-30, -43.61) * mm});
            skPoint(sketch, "E321.0", {"position": v(-30, 20.97) * mm});
            skLineSegment(sketch, "E322.0.1.0", {"start": v(-26, 23.97) * mm, "end": v(-26, 28.97) * mm});
            skLineSegment(sketch, "E322.0.1.1", {"start": v(-26, 23.97) * mm, "end": v(-21, 23.97) * mm});
            skLineSegment(sketch, "E322.0.1.2", {"start": v(-26, 28.97) * mm, "end": v(-21, 28.97) * mm});
            skLineSegment(sketch, "E322.0.1.3", {"start": v(-21, 23.97) * mm, "end": v(-21, 28.97) * mm});
            skLineSegment(sketch, "E322.0.1.4", {"start": v(-2.5, 42.57) * mm, "end": v(-2.5, 47.57) * mm});
            skLineSegment(sketch, "E322.0.1.5", {"start": v(0, 42.57) * mm, "end": v(-2.5, 42.57) * mm});
            skLineSegment(sketch, "E322.0.1.6", {"start": v(0, 42.57) * mm, "end": v(2.5, 42.57) * mm});
            skLineSegment(sketch, "E322.0.1.7", {"start": v(2.5, 42.57) * mm, "end": v(2.5, 47.57) * mm});
            skLineSegment(sketch, "E322.0.1.8", {"start": v(0, 47.57) * mm, "end": v(2.5, 47.57) * mm});
            skLineSegment(sketch, "E322.0.1.9", {"start": v(0, 47.57) * mm, "end": v(-2.5, 47.57) * mm});
            skLineSegment(sketch, "E322.0.1.10", {"start": v(21, 23.97) * mm, "end": v(21, 28.97) * mm});
            skLineSegment(sketch, "E322.0.1.11", {"start": v(26, 23.97) * mm, "end": v(21, 23.97) * mm});
            skLineSegment(sketch, "E322.0.1.12", {"start": v(26, 28.97) * mm, "end": v(21, 28.97) * mm});
            skLineSegment(sketch, "E322.0.1.13", {"start": v(26, 23.97) * mm, "end": v(26, 28.97) * mm});
            skLineSegment(sketch, "E322.direction1", {"start": v(-26, -40.61) * mm, "end": v(-1, -40.61) * mm, "construction": true});
            skLineSegment(sketch, "E322.direction2", {"start": v(-26, -40.61) * mm, "end": v(-26, 23.97) * mm, "construction": true});
            skSolve(sketch);
        }
        {
            var Q0;
            Q0=makeQuery(id+"F9.imprint","IMPRINT",FACE,{"disambiguationData":[TD([[makeQuery(id+"F9.imprint","IMPRINT",EDGE,{"derivedFrom":sQuery(id+"F9.wireOp",EDGE,"E311.bottom")}),1.0]])]});
            var Q1;
            Q1=makeQuery(id+"F9.imprint","IMPRINT",FACE,{"disambiguationData":[TD([[makeQuery(id+"F9.imprint","IMPRINT",EDGE,{"derivedFrom":sQuery(id+"F9.wireOp",EDGE,"E316.MirrorCS")}),1.0]])]});
            var Q2;
            Q2=makeQuery(id+"F9.imprint","IMPRINT",FACE,{"disambiguationData":[TD([[makeQuery(id+"F9.imprint","IMPRINT",EDGE,{"derivedFrom":sQuery(id+"F9.wireOp",EDGE,"E322.0.1.0")}),-1.0]])]});
            var Q3;
            Q3=makeQuery(id+"F9.imprint","IMPRINT",FACE,{"disambiguationData":[TD([[makeQuery(id+"F9.imprint","IMPRINT",EDGE,{"derivedFrom":sQuery(id+"F9.wireOp",EDGE,"E322.0.1.10")}),-1.0]])]});
            extrude(context, id + "F10", {"entities" : qUnion([Q0, Q1, Q2, Q3]), "operationType" : NewBodyOperationType.REMOVE, "depth" : 2.5 * mm, "offsetDistance" : 25 * mm});
        }
    });
